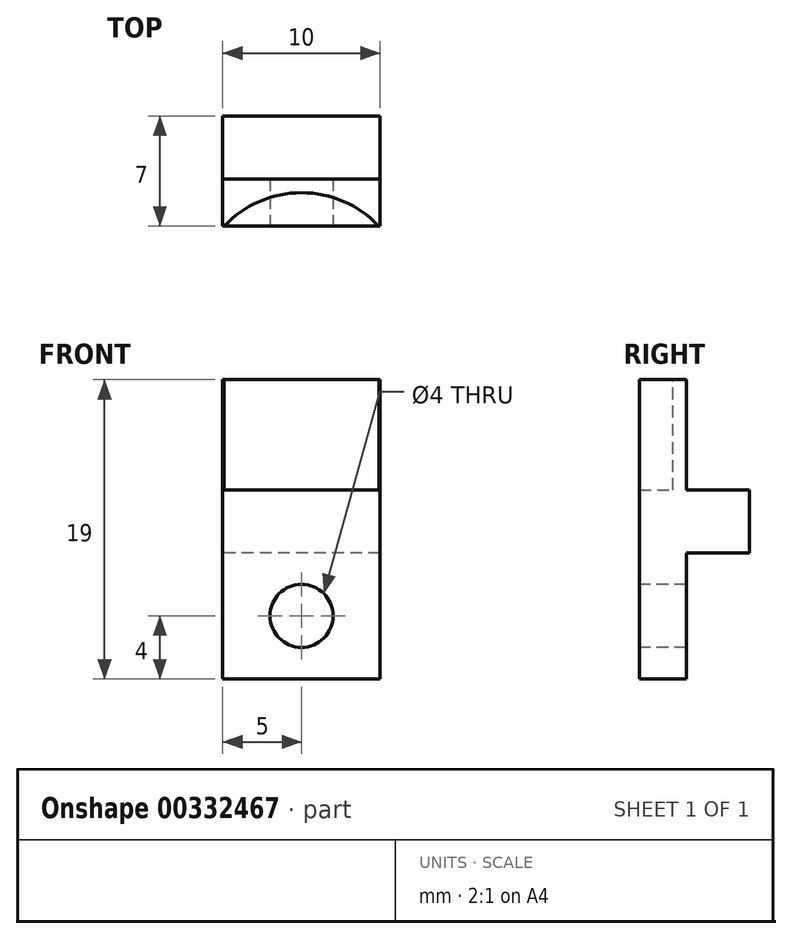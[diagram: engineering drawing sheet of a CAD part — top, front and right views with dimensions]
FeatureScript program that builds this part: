
annotation { "Feature Type Name" : "Feature", "Feature Type Description" : "" }
export const myFeature = defineFeature(function(context is Context, id is Id, definition is map)
    precondition{}
    {
        {
            var Q0;
            Q0=qCreatedBy(makeId("Top.planeOp"),FACE);
            var sketch = newSketch(context, id + "F0", { "sketchPlane" : qUnion([Q0])});
            skLineSegment(sketch, "E0.bottom", {"start": v(5, -3.5) * mm, "end": v(-5, -3.5) * mm});
            skLineSegment(sketch, "E0.top", {"start": v(5, 3.5) * mm, "end": v(-5, 3.5) * mm});
            skLineSegment(sketch, "E0.left", {"start": v(5, -3.5) * mm, "end": v(5, 3.5) * mm});
            skLineSegment(sketch, "E0.right", {"start": v(-5, -3.5) * mm, "end": v(-5, 3.5) * mm});
            skPoint(sketch, "E0.middle", {"position": v(0, 0) * mm});
            skSolve(sketch);
        }
        {
            var Q0;
            Q0 = qSketchRegion(id + "F0", true);
            extrude(context, id + "F1", {"entities" : qUnion([Q0]), "depth" : 19 * mm});
        }
        {
            var Q0;
            Q0=makeQuery(id+"F1.opExtrude","CAP_FACE",FACE,{"disambiguationData":[OSD([sQuery(id+"F0.wireOp",EDGE,"E0.bottom"),sQuery(id+"F0.wireOp",EDGE,"E0.top"),sQuery(id+"F0.wireOp",EDGE,"E0.left"),sQuery(id+"F0.wireOp",EDGE,"E0.right")])],"isStart":false});
            var sketch = newSketch(context, id + "F2", { "sketchPlane" : qUnion([Q0])});
            skArc(sketch, "E1", {"start": v(4.92, -3.5) * mm, "mid": v(0, -1.37) * mm, "end": v(-4.92, -3.5) * mm});
            skLineSegment(sketch, "E2.0", {"start": v(5, -3.5) * mm, "end": v(-5, -3.5) * mm});
            skLineSegment(sketch, "E3.0", {"start": v(5, -3.5) * mm, "end": v(5, 3.5) * mm});
            skLineSegment(sketch, "E4.0", {"start": v(5, 3.5) * mm, "end": v(-5, 3.5) * mm});
            skLineSegment(sketch, "E5.0", {"start": v(-5, -3.5) * mm, "end": v(-5, 3.5) * mm});
            skLineSegment(sketch, "E6", {"start": v(5, -0.5) * mm, "end": v(-5, -0.5) * mm});
            skSolve(sketch);
        }
        {
            var Q0;
            {var subQ0=sQuery(id+"F2.wireOp",EDGE,"E1");Q0=makeQuery(id+"F2.imprint","IMPRINT",FACE,{"disambiguationData":[TD([[makeQuery(id+"F2.imprint","IMPRINT",EDGE,{"derivedFrom":subQ0}),1.0]])]});}
            var Q1;
            {var subQ0=sQuery(id+"F2.wireOp",EDGE,"E4.0");Q1=makeQuery(id+"F2.imprint","IMPRINT",FACE,{"disambiguationData":[TD([[makeQuery(id+"F2.imprint","IMPRINT",EDGE,{"derivedFrom":subQ0}),1.0]])]});}
            extrude(context, id + "F3", {"entities" : qUnion([Q0, Q1]), "operationType" : NewBodyOperationType.REMOVE, "oppositeDirection" : true, "depth" : 7 * mm});
        }
        {
            var Q0;
            Q0=makeQuery(id+"F1.opExtrude","SWEPT_FACE",FACE,{"disambiguationData":[OSD([sQuery(id+"F0.wireOp",EDGE,"E0.bottom")])]});
            var sketch = newSketch(context, id + "F4", { "sketchPlane" : qUnion([Q0])});
            skLineSegment(sketch, "E7", {"start": v(5, 8) * mm, "end": v(-5, 8) * mm});
            skCircle(sketch, "E8", {"center": v(0, 4) * mm, "radius": 2 * mm});
            skPoint(sketch, "E8.centerSnap0", {"position": v(0, 8) * mm});
            skSolve(sketch);
        }
        {
            var Q0;
            Q0=makeQuery(id+"F4.imprint","IMPRINT",FACE,{"disambiguationData":[TD([[makeQuery(id+"F4.imprint","IMPRINT",EDGE,{"derivedFrom":sQuery(id+"F4.wireOp",EDGE,"E8")}),1.0]])]});
            extrude(context, id + "F5", {"entities" : qUnion([Q0]), "operationType" : NewBodyOperationType.REMOVE, "endBound" : BoundingType.THROUGH_ALL, "oppositeDirection" : true, "depth" : 25 * mm});
        }
        {
            var Q0;
            Q0=makeQuery(id+"F1.opExtrude","SWEPT_FACE",FACE,{"disambiguationData":[OSD([sQuery(id+"F0.wireOp",EDGE,"E0.top")])]});
            var sketch = newSketch(context, id + "F6", { "sketchPlane" : qUnion([Q0])});
            skLineSegment(sketch, "E9.0", {"start": v(-5, 0) * mm, "end": v(5, 0) * mm});
            skLineSegment(sketch, "E10.0", {"start": v(-5, 8) * mm, "end": v(-5, 0) * mm});
            skLineSegment(sketch, "E11.0", {"start": v(5, 8) * mm, "end": v(5, 0) * mm});
            skLineSegment(sketch, "E12", {"start": v(-5, 8) * mm, "end": v(5, 8) * mm});
            skPoint(sketch, "E13.orphan", {"position": v(-5, 12) * mm});
            skPoint(sketch, "E14.orphan", {"position": v(5, 12) * mm});
            skSolve(sketch);
        }
        {
            var Q0;
            Q0 = qSketchRegion(id + "F6", true);
            extrude(context, id + "F7", {"entities" : qUnion([Q0]), "operationType" : NewBodyOperationType.REMOVE, "oppositeDirection" : true, "depth" : 4 * mm});
        }
    });
